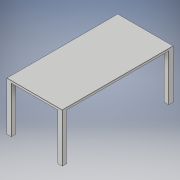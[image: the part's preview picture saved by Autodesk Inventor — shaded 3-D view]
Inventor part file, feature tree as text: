
AUTODESK INVENTOR PART (.ipt)
format: ipt  version: 2018 (Build 220112000, 112)  size: 157,184 bytes
history: native  units: in
note: dims shown in document units (in); Inventor stores cm internally (conversion verified against a paired STEP export)
features: extrude x2, sketch x2, fillet x1
ambient origin geometry x8: Origin, YZ Plane, XZ Plane, XY Plane, X Axis, Y Axis, Z Axis, Center Point
bodies: Solid1 (feature_tree)
feature tree (5):
  extrude  "Extrusion1"  Depth=36.0in
  extrude  "Extrusion2"  Depth=3.0in
  fillet  "Fillet1"  Radius=3.0in
  sketch  "Sketch1"  dims[d0=72.0in d1=36.0in]
  sketch  "Sketch2"  dims[d2=1.5in d3=0.0in d4=3.0in d5=3.0in d6=3.0in d7=3.0in d8=3.0in d9=3.0in d10=3.0in d11=3.0in d12=30.0in d13=0.0in d14=0.125in]
